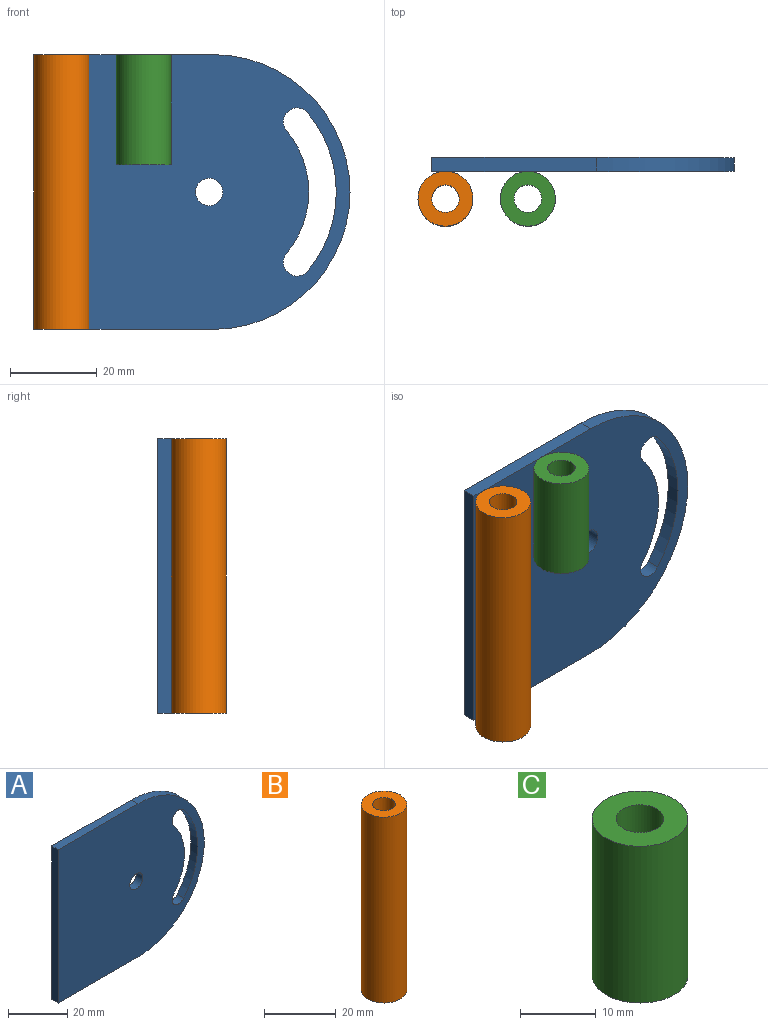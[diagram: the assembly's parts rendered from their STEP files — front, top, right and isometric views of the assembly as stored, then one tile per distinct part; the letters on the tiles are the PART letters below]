
ASSEMBLY  parts=3 mates=2
PART A: 11 faces, bbox 69.9x3.2x63.5 mm
  f0: cylinder r=31.75mm len=63.5mm, axis (0,1,0), area 316.7mm2, adj f1,f7,f8,f9
  f1: plane 38.1x3.18mm, normal (0,0,1), area 121mm2, adj f0,f2,f8,f9
  f2: plane 63.5x3.18mm, normal (-1,0,0), area 201.6mm2, adj f1,f7,f8,f9
  f3: cylinder r=3.17mm len=5.61mm, axis (0,1,0), area 31.7mm2, adj f4,f6,f8,f9
  f4: cylinder r=28.57mm len=36.59mm, axis (0,1,0), area 126.1mm2, adj f3,f5,f8,f9
  f5: cylinder r=3.17mm len=5.61mm, axis (0,1,0), area 31.7mm2, adj f4,f6,f8,f9
  f6: cylinder r=22.23mm len=28.46mm, axis (0,1,0), area 98mm2, adj f3,f5,f8,f9
  f7: plane 38.1x3.18mm, normal (0,0,-1), area 121mm2, adj f0,f2,f8,f9
  f8: plane 69.85x63.5mm, normal (0,-1,0), area 3715.4mm2, adj f0,f1,f2,f3,f4,f5,f6,f7
  f9: plane 69.85x63.5mm, normal (0,1,0), area 3715.4mm2, adj f0,f1,f2,f3,f4,f5,f6,f7
  f10: cylinder r=3.17mm len=6.35mm, axis (0,1,0), area 63.3mm2, adj f8,f9
PART B: 4 faces, bbox 12.7x12.7x63.5 mm
  f0: cylinder r=3.17mm len=63.5mm, axis (0,0,-1), area 1266.8mm2, adj f2,f3
  f1: cylinder r=6.35mm len=63.5mm, axis (0,0,-1), area 2533.5mm2, adj f2,f3
  f2: plane 12.7x12.7mm, normal (0,0,1), area 95mm2, adj f0,f1
  f3: plane 12.7x12.7mm, normal (0,0,-1), area 95mm2, adj f0,f1
PART C: 4 faces, bbox 12.7x12.7x25.4 mm
  f0: cylinder r=3.17mm len=25.4mm, axis (0,0,-1), area 506.7mm2, adj f2,f3
  f1: cylinder r=6.35mm len=25.4mm, axis (0,0,-1), area 1013.4mm2, adj f2,f3
  f2: plane 12.7x12.7mm, normal (0,0,1), area 95mm2, adj f0,f1
  f3: plane 12.7x12.7mm, normal (0,0,-1), area 95mm2, adj f0,f1
PLACE A rot(axis=(0.97,0.2,0.13),0deg) t=(1.73,34.19,-9.31)mm
PLACE B rot(axis=(0,0,1),90deg) t=(4.9,24.66,-9.31)mm
PLACE C rot(axis=(0,0,1),90deg) t=(23.95,24.66,28.79)mm
MATE fastened B.f2 <-> A.f1  axis (0,0,1) through (4.9,31.01,54.19)mm
MATE fastened C.f2 <-> A.f1  axis (0,0,1) through (23.95,31.01,54.19)mm
